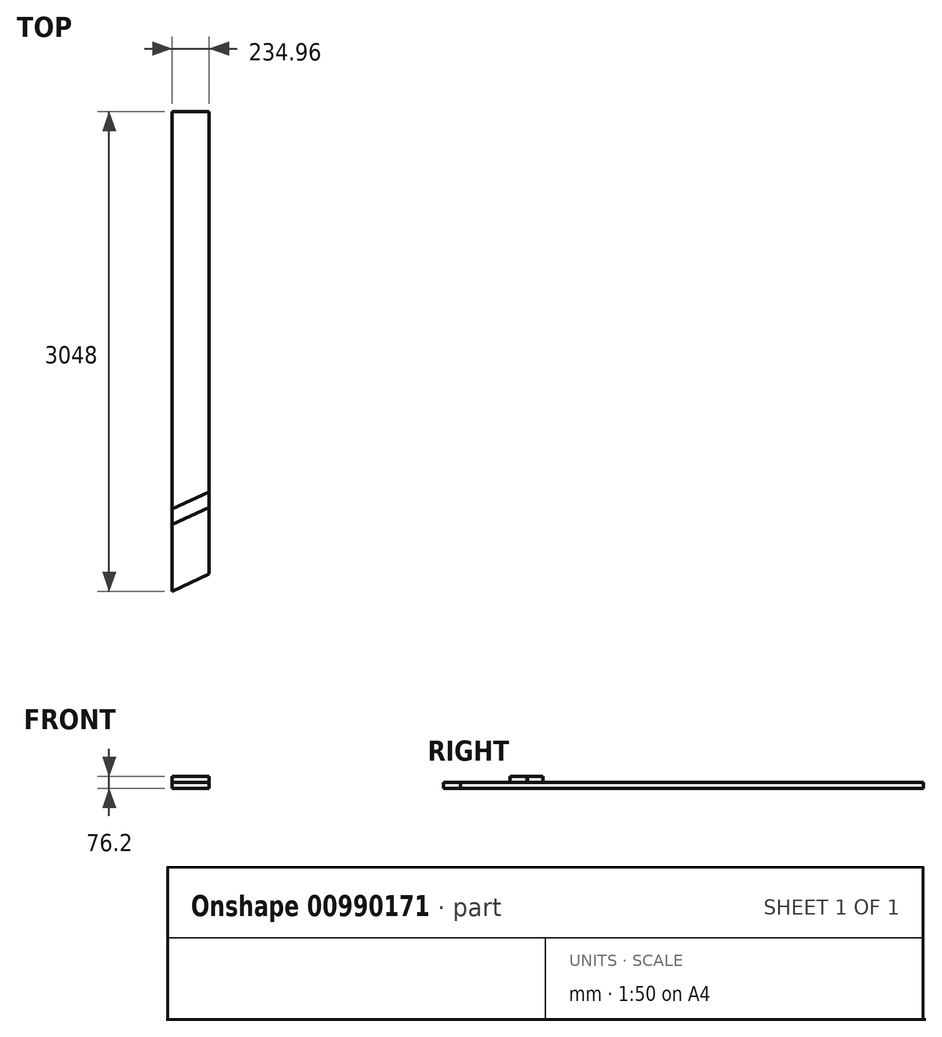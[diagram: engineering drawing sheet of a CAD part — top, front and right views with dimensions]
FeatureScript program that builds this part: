
annotation { "Feature Type Name" : "Feature", "Feature Type Description" : "" }
export const myFeature = defineFeature(function(context is Context, id is Id, definition is map)
    precondition{}
    {
        {
            assignVariable(context, id + "F0", {"name" : "w", "anyValue" : 38.1 * mm});
        }
        {
            var Q0;
            Q0=qCreatedBy(makeId("Top.planeOp"),FACE);
            var sketch = newSketch(context, id + "F1", { "sketchPlane" : qUnion([Q0])});
            skLineSegment(sketch, "E0.bottom", {"start": v(117.47, 1524) * mm, "end": v(-117.48, 1524) * mm});
            skLineSegment(sketch, "E0.top", {"start": v(117.47, -1524) * mm, "end": v(-117.48, -1524) * mm});
            skLineSegment(sketch, "E0.left", {"start": v(117.47, 1524) * mm, "end": v(117.47, -1524) * mm});
            skLineSegment(sketch, "E0.right", {"start": v(-117.48, 1524) * mm, "end": v(-117.48, -1524) * mm});
            skPoint(sketch, "E0.middle", {"position": v(0, 0) * mm});
            skSolve(sketch);
        }
        {
            var Q0;
            Q0=qSketchRegion(id+"F1",true);
            extrude(context, id + "F2", {"entities" : qUnion([Q0]), "depth" : getVariable(context, 'w'), "offsetDistance" : 25.4 * mm});
        }
        {
            var Q0;
            Q0=makeQuery(id+"F2.opExtrude","CAP_FACE",FACE,{"disambiguationData":[OSD([sQuery(id+"F1.wireOp",EDGE,"E0.bottom"),sQuery(id+"F1.wireOp",EDGE,"E0.top"),sQuery(id+"F1.wireOp",EDGE,"E0.left"),sQuery(id+"F1.wireOp",EDGE,"E0.right")])],"isStart":false});
            var sketch = newSketch(context, id + "F3", { "sketchPlane" : qUnion([Q0])});
            skLineSegment(sketch, "E1", {"start": v(-117.48, -1524) * mm, "end": v(117.47, -1414.44) * mm});
            skLineSegment(sketch, "E2", {"start": v(117.47, -1414.44) * mm, "end": v(117.47, -1524) * mm});
            skLineSegment(sketch, "E3", {"start": v(117.47, -1524) * mm, "end": v(-117.48, -1524) * mm});
            skSolve(sketch);
        }
        {
            var Q0;
            Q0 = qSketchRegion(id + "F3", true);
            extrude(context, id + "F4", {"entities" : qUnion([Q0]), "operationType" : NewBodyOperationType.REMOVE, "endBound" : BoundingType.UP_TO_NEXT, "oppositeDirection" : true, "depth" : 25.4 * mm, "offsetDistance" : 25.4 * mm});
        }
        {
            var Q0;
            Q0=makeQuery(id+"F2.opExtrude","CAP_FACE",FACE,{"disambiguationData":[OSD([sQuery(id+"F1.wireOp",EDGE,"E0.bottom"),sQuery(id+"F1.wireOp",EDGE,"E0.top"),sQuery(id+"F1.wireOp",EDGE,"E0.left"),sQuery(id+"F1.wireOp",EDGE,"E0.right")])],"isStart":false});
            var sketch = newSketch(context, id + "F5", { "sketchPlane" : qUnion([Q0])});
            skLineSegment(sketch, "E4", {"start": v(-117.48, -1099.8) * mm, "end": v(117.47, -990.24) * mm});
            skLineSegment(sketch, "E5", {"start": v(-117.48, -1099.8) * mm, "end": v(-117.48, -1001.7) * mm});
            skLineSegment(sketch, "E6", {"start": v(-117.48, -1001.7) * mm, "end": v(117.47, -892.14) * mm});
            skLineSegment(sketch, "E7", {"start": v(117.47, -892.14) * mm, "end": v(117.47, -990.24) * mm});
            skLineSegment(sketch, "E8", {"start": v(28.34, -1031.8) * mm, "end": v(-9.24, -951.23) * mm});
            skSolve(sketch);
        }
        {
            var Q0;
            Q0 = qSketchRegion(id + "F5", true);
            extrude(context, id + "F6", {"entities" : qUnion([Q0]), "depth" : 38.1 * mm, "offsetDistance" : 25.4 * mm});
        }
    });
